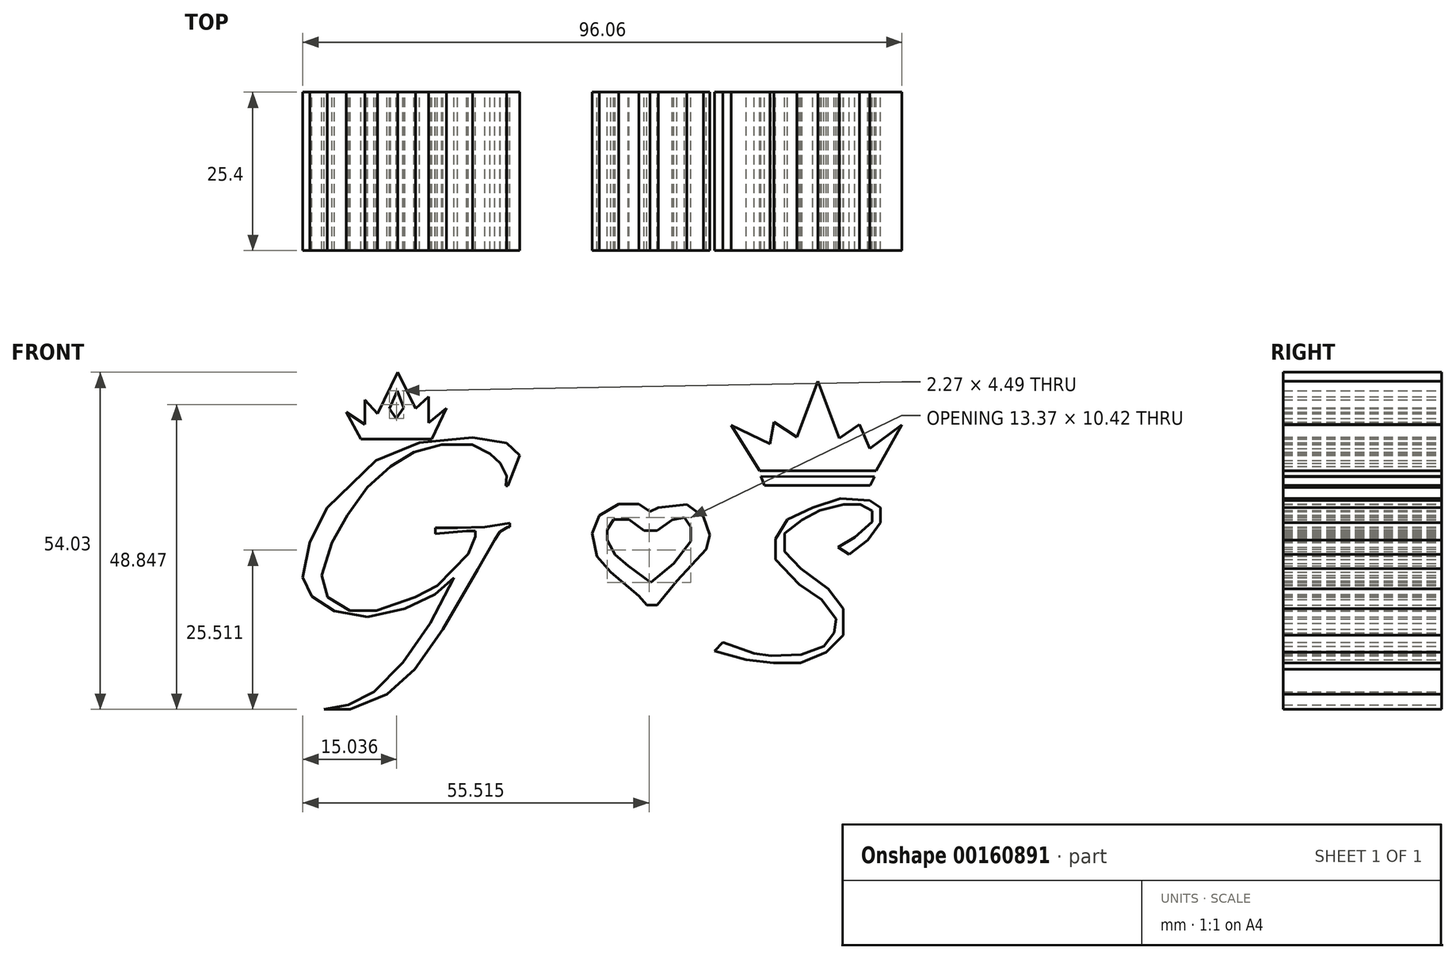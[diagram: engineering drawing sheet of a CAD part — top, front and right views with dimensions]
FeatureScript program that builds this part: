
annotation { "Feature Type Name" : "Feature", "Feature Type Description" : "" }
export const myFeature = defineFeature(function(context is Context, id is Id, definition is map)
    precondition{}
    {
        {
            var Q0;
            Q0=qCreatedBy(makeId("Front.planeOp"),FACE);
            var sketch = newSketch(context, id + "F0", { "sketchPlane" : qUnion([Q0])});
            skLineSegment(sketch, "E0", {"start": v(-12.47, 3.44) * mm, "end": v(-10.58, 8.35) * mm});
            skLineSegment(sketch, "E1", {"start": v(-10.58, 8.35) * mm, "end": v(-12.69, 10.3) * mm});
            skLineSegment(sketch, "E2", {"start": v(-12.69, 10.3) * mm, "end": v(-18.13, 11.22) * mm});
            skLineSegment(sketch, "E3", {"start": v(-18.13, 11.22) * mm, "end": v(-26.67, 10.4) * mm});
            skLineSegment(sketch, "E4", {"start": v(-26.67, 10.4) * mm, "end": v(-33.65, 7.52) * mm});
            skLineSegment(sketch, "E5", {"start": v(-33.65, 7.52) * mm, "end": v(-41.46, 0) * mm});
            skLineSegment(sketch, "E6", {"start": v(-41.46, 0) * mm, "end": v(-44.24, -5.53) * mm});
            skLineSegment(sketch, "E7", {"start": v(-44.24, -5.53) * mm, "end": v(-45.37, -11.18) * mm});
            skLineSegment(sketch, "E8", {"start": v(-45.37, -11.18) * mm, "end": v(-43.93, -14.27) * mm});
            skLineSegment(sketch, "E9", {"start": v(-43.93, -14.27) * mm, "end": v(-40.33, -16.63) * mm});
            skLineSegment(sketch, "E10", {"start": v(-40.33, -16.63) * mm, "end": v(-34.99, -17.55) * mm});
            skLineSegment(sketch, "E11", {"start": v(-34.99, -17.55) * mm, "end": v(-29.03, -16.22) * mm});
            skLineSegment(sketch, "E12", {"start": v(-29.03, -16.22) * mm, "end": v(-24.2, -13.96) * mm});
            skLineSegment(sketch, "E13", {"start": v(-24.2, -13.96) * mm, "end": v(-21.12, -11.29) * mm});
            skLineSegment(sketch, "E14", {"start": v(-21.12, -11.29) * mm, "end": v(-24.92, -18.58) * mm});
            skLineSegment(sketch, "E15", {"start": v(-24.92, -18.58) * mm, "end": v(-29.34, -24.85) * mm});
            skLineSegment(sketch, "E16", {"start": v(-29.34, -24.85) * mm, "end": v(-33.96, -29.58) * mm});
            skLineSegment(sketch, "E17", {"start": v(-33.96, -29.58) * mm, "end": v(-38.1, -31.64) * mm});
            skLineSegment(sketch, "E18", {"start": v(-38.1, -31.64) * mm, "end": v(-41.97, -32.36) * mm});
            skLineSegment(sketch, "E19", {"start": v(-41.97, -32.36) * mm, "end": v(-37.79, -32.36) * mm});
            skLineSegment(sketch, "E20", {"start": v(-37.79, -32.36) * mm, "end": v(-31.84, -29.95) * mm});
            skLineSegment(sketch, "E21", {"start": v(-31.84, -29.95) * mm, "end": v(-27.42, -25.93) * mm});
            skLineSegment(sketch, "E22", {"start": v(-27.42, -25.93) * mm, "end": v(-22.92, -19.5) * mm});
            skLineSegment(sketch, "E23", {"start": v(-22.92, -19.5) * mm, "end": v(-17.3, -9.94) * mm});
            skLineSegment(sketch, "E24", {"start": v(-17.3, -9.94) * mm, "end": v(-14.56, -5.2) * mm});
            skLineSegment(sketch, "E25", {"start": v(-14.56, -5.2) * mm, "end": v(-13.76, -3.91) * mm});
            skLineSegment(sketch, "E26", {"start": v(-13.76, -3.91) * mm, "end": v(-12.47, -3.11) * mm});
            skLineSegment(sketch, "E27", {"start": v(-12.47, -3.11) * mm, "end": v(-12.17, -3.11) * mm});
            skLineSegment(sketch, "E28", {"start": v(-12.17, -3.11) * mm, "end": v(-12.17, -2.48) * mm});
            skLineSegment(sketch, "E29", {"start": v(-12.17, -2.48) * mm, "end": v(-16.18, -3.14) * mm});
            skLineSegment(sketch, "E30", {"start": v(-16.18, -3.14) * mm, "end": v(-20.57, -3.28) * mm});
            skLineSegment(sketch, "E31", {"start": v(-20.57, -3.28) * mm, "end": v(-24.1, -3.28) * mm});
            skLineSegment(sketch, "E32", {"start": v(-24.1, -3.28) * mm, "end": v(-24.1, -4.25) * mm});
            skLineSegment(sketch, "E33", {"start": v(-24.1, -4.25) * mm, "end": v(-19.11, -3.78) * mm});
            skLineSegment(sketch, "E34", {"start": v(-19.11, -3.78) * mm, "end": v(-17.72, -3.78) * mm});
            skLineSegment(sketch, "E35", {"start": v(-17.72, -3.78) * mm, "end": v(-17.72, -4.66) * mm});
            skLineSegment(sketch, "E36", {"start": v(-17.72, -4.66) * mm, "end": v(-18.82, -7.44) * mm});
            skLineSegment(sketch, "E37", {"start": v(-18.82, -7.44) * mm, "end": v(-23.82, -12.55) * mm});
            skLineSegment(sketch, "E38", {"start": v(-23.82, -12.55) * mm, "end": v(-27.36, -14.4) * mm});
            skLineSegment(sketch, "E39", {"start": v(-27.36, -14.4) * mm, "end": v(-33.57, -16.55) * mm});
            skLineSegment(sketch, "E40", {"start": v(-33.57, -16.55) * mm, "end": v(-37.8, -16.55) * mm});
            skLineSegment(sketch, "E41", {"start": v(-37.8, -16.55) * mm, "end": v(-41.4, -14.4) * mm});
            skLineSegment(sketch, "E42", {"start": v(-41.4, -14.4) * mm, "end": v(-42.33, -10.87) * mm});
            skLineSegment(sketch, "E43", {"start": v(-42.33, -10.87) * mm, "end": v(-40.7, -5.64) * mm});
            skLineSegment(sketch, "E44", {"start": v(-40.7, -5.64) * mm, "end": v(-38.21, -1.23) * mm});
            skLineSegment(sketch, "E45", {"start": v(-38.21, -1.23) * mm, "end": v(-35.02, 3.18) * mm});
            skLineSegment(sketch, "E46", {"start": v(-35.02, 3.18) * mm, "end": v(-31.3, 6.6) * mm});
            skLineSegment(sketch, "E47", {"start": v(-31.3, 6.6) * mm, "end": v(-27.52, 8.86) * mm});
            skLineSegment(sketch, "E48", {"start": v(-27.52, 8.86) * mm, "end": v(-23.1, 10.1) * mm});
            skLineSegment(sketch, "E49", {"start": v(-23.1, 10.1) * mm, "end": v(-18.22, 10.1) * mm});
            skLineSegment(sketch, "E50", {"start": v(-18.22, 10.1) * mm, "end": v(-15.34, 8.63) * mm});
            skLineSegment(sketch, "E51", {"start": v(-15.34, 8.63) * mm, "end": v(-13.7, 7.1) * mm});
            skLineSegment(sketch, "E52", {"start": v(-13.7, 7.1) * mm, "end": v(-12.7, 5.04) * mm});
            skLineSegment(sketch, "E53", {"start": v(-12.7, 5.04) * mm, "end": v(-12.82, 3.48) * mm});
            skLineSegment(sketch, "E54", {"start": v(-12.82, 3.48) * mm, "end": v(-12.47, 3.44) * mm});
            skSolve(sketch);
        }
        {
            var Q0;
            Q0=makeQuery(id+"F0.imprint","IMPRINT",FACE,{"disambiguationData":[TD([[makeQuery(id+"F0.imprint","IMPRINT",EDGE,{"derivedFrom":sQuery(id+"F0.wireOp",EDGE,"E0")}),1.0]])]});
            extrude(context, id + "F1", {"entities" : qUnion([Q0]), "depth" : 25.4 * mm});
        }
        {
            var Q0;
            Q0=qCreatedBy(makeId("Front.planeOp"),FACE);
            var sketch = newSketch(context, id + "F2", { "sketchPlane" : qUnion([Q0])});
            skLineSegment(sketch, "E55", {"start": v(40.48, -6.4) * mm, "end": v(42.21, -7.55) * mm});
            skLineSegment(sketch, "E56", {"start": v(42.21, -7.55) * mm, "end": v(45.2, -5.24) * mm});
            skLineSegment(sketch, "E57", {"start": v(45.2, -5.24) * mm, "end": v(47.28, -2.41) * mm});
            skLineSegment(sketch, "E58", {"start": v(47.28, -2.41) * mm, "end": v(47.28, 0) * mm});
            skLineSegment(sketch, "E59", {"start": v(47.28, 0) * mm, "end": v(45.52, 1.08) * mm});
            skLineSegment(sketch, "E60", {"start": v(45.52, 1.08) * mm, "end": v(40.83, 1.44) * mm});
            skLineSegment(sketch, "E61", {"start": v(40.83, 1.44) * mm, "end": v(36.4, 0) * mm});
            skLineSegment(sketch, "E62", {"start": v(36.4, 0) * mm, "end": v(32.36, -1.96) * mm});
            skLineSegment(sketch, "E63", {"start": v(32.36, -1.96) * mm, "end": v(30.44, -5.08) * mm});
            skLineSegment(sketch, "E64", {"start": v(30.44, -5.08) * mm, "end": v(30.44, -8.35) * mm});
            skLineSegment(sketch, "E65", {"start": v(30.44, -8.35) * mm, "end": v(34.26, -12.33) * mm});
            skLineSegment(sketch, "E66", {"start": v(34.26, -12.33) * mm, "end": v(37.82, -14.76) * mm});
            skLineSegment(sketch, "E67", {"start": v(37.82, -14.76) * mm, "end": v(40.13, -17.84) * mm});
            skLineSegment(sketch, "E68", {"start": v(40.13, -17.84) * mm, "end": v(39.8, -20.07) * mm});
            skLineSegment(sketch, "E69", {"start": v(39.8, -20.07) * mm, "end": v(38.16, -22.27) * mm});
            skLineSegment(sketch, "E70", {"start": v(38.16, -22.27) * mm, "end": v(34.55, -23.6) * mm});
            skLineSegment(sketch, "E71", {"start": v(34.55, -23.6) * mm, "end": v(29.72, -23.8) * mm});
            skLineSegment(sketch, "E72", {"start": v(29.72, -23.8) * mm, "end": v(27.01, -23.43) * mm});
            skLineSegment(sketch, "E73", {"start": v(27.01, -23.43) * mm, "end": v(21.99, -21.61) * mm});
            skLineSegment(sketch, "E74", {"start": v(21.99, -21.61) * mm, "end": v(20.68, -23.02) * mm});
            skLineSegment(sketch, "E75", {"start": v(20.68, -23.02) * mm, "end": v(25.75, -24.42) * mm});
            skLineSegment(sketch, "E76", {"start": v(25.75, -24.42) * mm, "end": v(30.1, -24.92) * mm});
            skLineSegment(sketch, "E77", {"start": v(30.1, -24.92) * mm, "end": v(34.42, -24.92) * mm});
            skLineSegment(sketch, "E78", {"start": v(34.42, -24.92) * mm, "end": v(38.53, -23.22) * mm});
            skLineSegment(sketch, "E79", {"start": v(38.53, -23.22) * mm, "end": v(41.3, -20.46) * mm});
            skLineSegment(sketch, "E80", {"start": v(41.3, -20.46) * mm, "end": v(41.3, -16.2) * mm});
            skLineSegment(sketch, "E81", {"start": v(41.3, -16.2) * mm, "end": v(38.88, -13.04) * mm});
            skLineSegment(sketch, "E82", {"start": v(38.88, -13.04) * mm, "end": v(34.47, -9.78) * mm});
            skLineSegment(sketch, "E83", {"start": v(34.47, -9.78) * mm, "end": v(31.91, -7.07) * mm});
            skLineSegment(sketch, "E84", {"start": v(31.91, -7.07) * mm, "end": v(31.91, -4.17) * mm});
            skLineSegment(sketch, "E85", {"start": v(31.91, -4.17) * mm, "end": v(34.67, -2) * mm});
            skLineSegment(sketch, "E86", {"start": v(34.67, -2) * mm, "end": v(37.53, -0.45) * mm});
            skLineSegment(sketch, "E87", {"start": v(37.53, -0.45) * mm, "end": v(41.34, 0.45) * mm});
            skLineSegment(sketch, "E88", {"start": v(41.34, 0.45) * mm, "end": v(44.05, 0.45) * mm});
            skLineSegment(sketch, "E89", {"start": v(44.05, 0.45) * mm, "end": v(45.95, -0.56) * mm});
            skLineSegment(sketch, "E90", {"start": v(45.95, -0.56) * mm, "end": v(45.95, -2.3) * mm});
            skLineSegment(sketch, "E91", {"start": v(45.95, -2.3) * mm, "end": v(43.15, -4.77) * mm});
            skLineSegment(sketch, "E92", {"start": v(43.15, -4.77) * mm, "end": v(40.48, -6.4) * mm});
            skSolve(sketch);
        }
        {
            var Q0;
            Q0=makeQuery(id+"F2.imprint","IMPRINT",FACE,{"disambiguationData":[TD([[makeQuery(id+"F2.imprint","IMPRINT",EDGE,{"derivedFrom":sQuery(id+"F2.wireOp",EDGE,"E55")}),1.0]])]});
            extrude(context, id + "F3", {"entities" : qUnion([Q0]), "depth" : 25.4 * mm});
        }
        {
            var Q0;
            Q0=qCreatedBy(makeId("Front.planeOp"),FACE);
            var sketch = newSketch(context, id + "F4", { "sketchPlane" : qUnion([Q0])});
            skLineSegment(sketch, "E93", {"start": v(-38.38, 15.28) * mm, "end": v(-36.06, 10.93) * mm});
            skLineSegment(sketch, "E94", {"start": v(-36.06, 10.93) * mm, "end": v(-24.7, 10.93) * mm});
            skLineSegment(sketch, "E95", {"start": v(-24.7, 10.93) * mm, "end": v(-22.34, 15.9) * mm});
            skLineSegment(sketch, "E96", {"start": v(-22.34, 15.9) * mm, "end": v(-25.18, 13.53) * mm});
            skLineSegment(sketch, "E97", {"start": v(-25.18, 13.53) * mm, "end": v(-25.18, 17.74) * mm});
            skLineSegment(sketch, "E98", {"start": v(-25.18, 17.74) * mm, "end": v(-27.26, 15.85) * mm});
            skLineSegment(sketch, "E99", {"start": v(-27.26, 15.85) * mm, "end": v(-30.15, 21.67) * mm});
            skLineSegment(sketch, "E100", {"start": v(-30.15, 21.67) * mm, "end": v(-33.4, 15.04) * mm});
            skLineSegment(sketch, "E101", {"start": v(-33.4, 15.04) * mm, "end": v(-35.44, 17.22) * mm});
            skLineSegment(sketch, "E102", {"start": v(-35.44, 17.22) * mm, "end": v(-35.44, 13.3) * mm});
            skLineSegment(sketch, "E103", {"start": v(-35.44, 13.3) * mm, "end": v(-38.38, 15.28) * mm});
            skLineSegment(sketch, "E104", {"start": v(-31.47, 15.85) * mm, "end": v(-30.43, 14.24) * mm});
            skLineSegment(sketch, "E105", {"start": v(-30.43, 14.24) * mm, "end": v(-29.2, 15.94) * mm});
            skLineSegment(sketch, "E106", {"start": v(-29.2, 15.94) * mm, "end": v(-30.24, 18.73) * mm});
            skLineSegment(sketch, "E107", {"start": v(-30.24, 18.73) * mm, "end": v(-31.47, 15.85) * mm});
            skSolve(sketch);
        }
        {
            var Q0;
            Q0=makeQuery(id+"F4.imprint","IMPRINT",FACE,{"disambiguationData":[TD([[makeQuery(id+"F4.imprint","IMPRINT",EDGE,{"derivedFrom":sQuery(id+"F4.wireOp",EDGE,"E93")}),1.0]])]});
            extrude(context, id + "F5", {"entities" : qUnion([Q0]), "depth" : 25.4 * mm});
        }
        {
            var Q0;
            Q0=qCreatedBy(makeId("Front.planeOp"),FACE);
            var sketch = newSketch(context, id + "F6", { "sketchPlane" : qUnion([Q0])});
            skLineSegment(sketch, "E108", {"start": v(23.3, 13.18) * mm, "end": v(27.9, 5.89) * mm});
            skLineSegment(sketch, "E109", {"start": v(27.9, 5.89) * mm, "end": v(46.6, 5.89) * mm});
            skLineSegment(sketch, "E110", {"start": v(46.6, 5.89) * mm, "end": v(50.69, 13.25) * mm});
            skLineSegment(sketch, "E111", {"start": v(50.69, 13.25) * mm, "end": v(45.57, 9.4) * mm});
            skLineSegment(sketch, "E112", {"start": v(45.57, 9.4) * mm, "end": v(43.9, 13.31) * mm});
            skLineSegment(sketch, "E113", {"start": v(43.9, 13.31) * mm, "end": v(40.64, 11.07) * mm});
            skLineSegment(sketch, "E114", {"start": v(40.64, 11.07) * mm, "end": v(37.25, 20.22) * mm});
            skLineSegment(sketch, "E115", {"start": v(37.25, 20.22) * mm, "end": v(33.85, 11.26) * mm});
            skLineSegment(sketch, "E116", {"start": v(33.85, 11.26) * mm, "end": v(30.2, 13.7) * mm});
            skLineSegment(sketch, "E117", {"start": v(30.2, 13.7) * mm, "end": v(29.57, 10.18) * mm});
            skLineSegment(sketch, "E118", {"start": v(29.57, 10.18) * mm, "end": v(23.3, 13.18) * mm});
            skLineSegment(sketch, "E119", {"start": v(28.1, 5) * mm, "end": v(28.67, 3.52) * mm});
            skLineSegment(sketch, "E120", {"start": v(28.67, 3.52) * mm, "end": v(45.63, 3.52) * mm});
            skLineSegment(sketch, "E121", {"start": v(45.63, 3.52) * mm, "end": v(46.33, 4.93) * mm});
            skLineSegment(sketch, "E122", {"start": v(46.33, 4.93) * mm, "end": v(28.1, 5) * mm});
            skSolve(sketch);
        }
        {
            var Q0;
            Q0=makeQuery(id+"F6.imprint","IMPRINT",FACE,{"disambiguationData":[TD([[makeQuery(id+"F6.imprint","IMPRINT",EDGE,{"derivedFrom":sQuery(id+"F6.wireOp",EDGE,"E108")}),1.0]])]});
            var Q1;
            Q1=makeQuery(id+"F6.imprint","IMPRINT",FACE,{"disambiguationData":[TD([[makeQuery(id+"F6.imprint","IMPRINT",EDGE,{"derivedFrom":sQuery(id+"F6.wireOp",EDGE,"E119")}),1.0]])]});
            extrude(context, id + "F7", {"entities" : qUnion([Q0, Q1]), "depth" : 25.4 * mm});
        }
        {
            var Q0;
            Q0=qCreatedBy(makeId("Front.planeOp"),FACE);
            var sketch = newSketch(context, id + "F8", { "sketchPlane" : qUnion([Q0])});
            skLineSegment(sketch, "E123", {"start": v(9.82, -15.67) * mm, "end": v(11.45, -15.67) * mm});
            skLineSegment(sketch, "E124", {"start": v(11.45, -15.67) * mm, "end": v(14.62, -11.8) * mm});
            skLineSegment(sketch, "E125", {"start": v(14.62, -11.8) * mm, "end": v(19.33, -6.7) * mm});
            skLineSegment(sketch, "E126", {"start": v(19.33, -6.7) * mm, "end": v(19.87, -4.41) * mm});
            skLineSegment(sketch, "E127", {"start": v(19.87, -4.41) * mm, "end": v(18.87, -1.48) * mm});
            skLineSegment(sketch, "E128", {"start": v(18.87, -1.48) * mm, "end": v(16.19, 0.5) * mm});
            skLineSegment(sketch, "E129", {"start": v(16.19, 0.5) * mm, "end": v(11.65, 0) * mm});
            skLineSegment(sketch, "E130", {"start": v(11.65, 0) * mm, "end": v(10.3, -0.65) * mm});
            skLineSegment(sketch, "E131", {"start": v(10.3, -0.65) * mm, "end": v(8.54, 0.53) * mm});
            skLineSegment(sketch, "E132", {"start": v(8.54, 0.53) * mm, "end": v(5.26, 0.53) * mm});
            skLineSegment(sketch, "E133", {"start": v(5.26, 0.53) * mm, "end": v(2.18, -1.3) * mm});
            skLineSegment(sketch, "E134", {"start": v(2.18, -1.3) * mm, "end": v(1.02, -4.17) * mm});
            skLineSegment(sketch, "E135", {"start": v(1.02, -4.17) * mm, "end": v(1.83, -7.85) * mm});
            skLineSegment(sketch, "E136", {"start": v(1.83, -7.85) * mm, "end": v(4.03, -10.4) * mm});
            skLineSegment(sketch, "E137", {"start": v(4.03, -10.4) * mm, "end": v(8.51, -14.22) * mm});
            skLineSegment(sketch, "E138", {"start": v(8.51, -14.22) * mm, "end": v(9.82, -15.67) * mm});
            skLineSegment(sketch, "E139", {"start": v(9.37, -3.7) * mm, "end": v(11.42, -3.7) * mm});
            skLineSegment(sketch, "E140", {"start": v(11.42, -3.7) * mm, "end": v(13.84, -2) * mm});
            skLineSegment(sketch, "E141", {"start": v(13.84, -2) * mm, "end": v(15.85, -1.64) * mm});
            skLineSegment(sketch, "E142", {"start": v(15.85, -1.64) * mm, "end": v(17.65, -2.54) * mm});
            skLineSegment(sketch, "E143", {"start": v(17.65, -2.54) * mm, "end": v(18.23, -4.92) * mm});
            skLineSegment(sketch, "E144", {"start": v(18.23, -4.92) * mm, "end": v(17.37, -7.14) * mm});
            skLineSegment(sketch, "E145", {"start": v(17.37, -7.14) * mm, "end": v(14.9, -9.64) * mm});
            skLineSegment(sketch, "E146", {"start": v(14.9, -9.64) * mm, "end": v(11.05, -13.37) * mm});
            skLineSegment(sketch, "E147", {"start": v(11.05, -13.37) * mm, "end": v(9.82, -15.67) * mm});
            skLineSegment(sketch, "E148", {"start": v(9.37, -3.7) * mm, "end": v(6.9, -1.93) * mm});
            skLineSegment(sketch, "E149", {"start": v(6.9, -1.93) * mm, "end": v(4.44, -1.93) * mm});
            skLineSegment(sketch, "E150", {"start": v(4.44, -1.93) * mm, "end": v(3.46, -3.57) * mm});
            skLineSegment(sketch, "E151", {"start": v(3.46, -3.57) * mm, "end": v(3.46, -5.2) * mm});
            skLineSegment(sketch, "E152", {"start": v(3.46, -5.2) * mm, "end": v(4.73, -7.59) * mm});
            skLineSegment(sketch, "E153", {"start": v(4.73, -7.59) * mm, "end": v(6.82, -9.35) * mm});
            skLineSegment(sketch, "E154", {"start": v(6.82, -9.35) * mm, "end": v(10.43, -12.06) * mm});
            skLineSegment(sketch, "E155", {"start": v(10.43, -12.06) * mm, "end": v(14.08, -8.98) * mm});
            skLineSegment(sketch, "E156", {"start": v(14.08, -8.98) * mm, "end": v(16.83, -5.41) * mm});
            skLineSegment(sketch, "E157", {"start": v(16.83, -5.41) * mm, "end": v(16.83, -3.16) * mm});
            skLineSegment(sketch, "E158", {"start": v(16.83, -3.16) * mm, "end": v(15.85, -1.64) * mm});
            skLineSegment(sketch, "E159", {"start": v(9.37, -3.7) * mm, "end": v(11.07, -1.31) * mm});
            skLineSegment(sketch, "E160", {"start": v(11.07, -1.31) * mm, "end": v(13.63, -0.37) * mm});
            skLineSegment(sketch, "E161", {"start": v(13.63, -0.37) * mm, "end": v(16.46, -0.37) * mm});
            skLineSegment(sketch, "E162", {"start": v(16.46, -0.37) * mm, "end": v(18.87, -1.48) * mm});
            skLineSegment(sketch, "E163", {"start": v(10.3, -0.65) * mm, "end": v(9.16, -1.56) * mm});
            skLineSegment(sketch, "E164", {"start": v(9.16, -1.56) * mm, "end": v(5.96, -0.7) * mm});
            skLineSegment(sketch, "E165", {"start": v(5.96, -0.7) * mm, "end": v(3.95, -1.56) * mm});
            skLineSegment(sketch, "E166", {"start": v(3.95, -1.56) * mm, "end": v(3.21, -2.91) * mm});
            skLineSegment(sketch, "E167", {"start": v(3.21, -2.91) * mm, "end": v(3.46, -5.2) * mm});
            skLineSegment(sketch, "E168", {"start": v(2.18, -1.3) * mm, "end": v(1.82, -3.4) * mm});
            skLineSegment(sketch, "E169", {"start": v(1.82, -3.4) * mm, "end": v(1.82, -5.04) * mm});
            skLineSegment(sketch, "E170", {"start": v(1.82, -5.04) * mm, "end": v(3.05, -7.3) * mm});
            skLineSegment(sketch, "E171", {"start": v(3.05, -7.3) * mm, "end": v(7.23, -11.44) * mm});
            skLineSegment(sketch, "E172", {"start": v(7.23, -11.44) * mm, "end": v(9.53, -13.5) * mm});
            skLineSegment(sketch, "E173", {"start": v(9.53, -13.5) * mm, "end": v(10.43, -12.06) * mm});
            skSolve(sketch);
        }
        {
            var Q0;
            Q0=makeQuery(id+"F8.imprint","IMPRINT",FACE,{"disambiguationData":[TD([[makeQuery(id+"F8.imprint","IMPRINT",EDGE,{"derivedFrom":sQuery(id+"F8.wireOp",EDGE,"E131")}),1.0]])]});
            var Q1;
            Q1=makeQuery(id+"F8.imprint","IMPRINT",FACE,{"disambiguationData":[TD([[makeQuery(id+"F8.imprint","IMPRINT",EDGE,{"derivedFrom":sQuery(id+"F8.wireOp",EDGE,"E123")}),1.0]])]});
            var Q2;
            Q2=makeQuery(id+"F8.imprint","IMPRINT",FACE,{"disambiguationData":[TD([[makeQuery(id+"F8.imprint","IMPRINT",EDGE,{"derivedFrom":sQuery(id+"F8.wireOp",EDGE,"E134")}),1.0]])]});
            var Q3;
            Q3=makeQuery(id+"F8.imprint","IMPRINT",FACE,{"disambiguationData":[TD([[makeQuery(id+"F8.imprint","IMPRINT",EDGE,{"derivedFrom":sQuery(id+"F8.wireOp",EDGE,"E128")}),1.0]])]});
            extrude(context, id + "F9", {"entities" : qUnion([Q0, Q1, Q2, Q3]), "depth" : 25.4 * mm});
        }
    });
